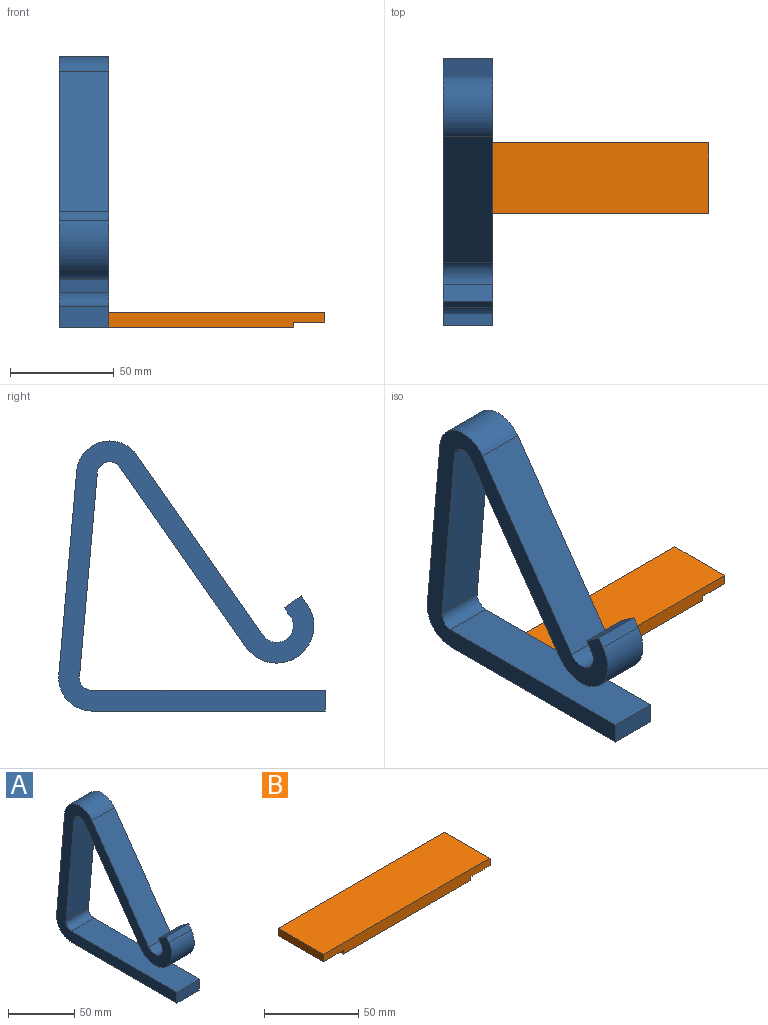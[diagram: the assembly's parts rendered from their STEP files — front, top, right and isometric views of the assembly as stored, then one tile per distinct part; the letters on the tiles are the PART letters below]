
ASSEMBLY  parts=2 mates=2
PART A: 28 faces, bbox 24x128.5x130.2 mm
  f0: plane 130.2x128.54mm, normal (1,0,0), area 3717.2mm2, adj f1,f2,f3,f4,f5,f6,f7,f8
  f1: plane 86.86x60.82mm, normal (0,0.82,-0.57), area 2545mm2, adj f0,f2,f13,f14
  f2: cylinder r=6mm len=24mm, axis (-1,0,0), area 351.9mm2, adj f0,f1,f3,f14
  f3: plane 98.2x24mm, normal (0,-1,-0.09), area 2365.9mm2, adj f0,f2,f4,f14
  f4: cylinder r=6mm len=24mm, axis (-1,0,0), area 238.8mm2, adj f0,f3,f5,f14
  f5: plane 112.54x24mm, normal (0,0,1), area 2700.9mm2, adj f0,f4,f6,f14
  f6: plane 24x10mm, normal (0,-1,0), area 240mm2, adj f0,f5,f7,f14
  f7: plane 112.54x24mm, normal (0,0,-1), area 2700.9mm2, adj f0,f6,f8,f14
  f8: cylinder r=16mm len=24mm, axis (-1,0,0), area 636.7mm2, adj f0,f7,f9,f14
  f9: plane 98.2x24mm, normal (0,1,0.09), area 2365.9mm2, adj f0,f8,f10,f14
  f10: cylinder r=16mm len=29.05mm, axis (-1,0,0), area 938.3mm2, adj f0,f9,f11,f14
  f11: plane 86.86x60.82mm, normal (0,-0.82,0.57), area 2545mm2, adj f0,f10,f12,f14
  f12: cylinder r=8mm len=24mm, axis (-1,0,0), area 603.2mm2, adj f0,f11,f14,f26
  f13: cylinder r=18mm len=32.74mm, axis (-1,0,0), area 1357.2mm2, adj f0,f1,f14,f25
  f14: plane 130.2x128.54mm, normal (-1,0,0), area 4081.2mm2, adj f1,f2,f3,f4,f5,f6,f7,f8
  f15: plane 34.87x20mm, normal (0,1,0.09), area 700mm2, adj f0,f16,f18,f19
  f16: plane 20x5.18mm, normal (0,-0.09,1), area 104mm2, adj f0,f15,f17,f19
  f17: plane 34.87x20mm, normal (0,-1,-0.09), area 700mm2, adj f0,f16,f18,f19
  f18: plane 20x5.18mm, normal (0,0.09,-1), area 104mm2, adj f0,f15,f17,f19
  f19: plane 35.32x8.23mm, normal (1,0,0), area 182mm2, adj f15,f16,f17,f18
  f20: plane 35x20mm, normal (0,0,-1), area 700mm2, adj f0,f21,f23,f24
  f21: plane 20x5.2mm, normal (0,1,0), area 104mm2, adj f0,f20,f22,f24
  f22: plane 35x20mm, normal (0,0,1), area 700mm2, adj f0,f21,f23,f24
  f23: plane 20x5.2mm, normal (0,-1,0), area 104mm2, adj f0,f20,f22,f24
  f24: plane 35x5.2mm, normal (1,0,0), area 182mm2, adj f20,f21,f22,f23
  f25: plane 24x4.1mm, normal (0,-0.82,0.57), area 120mm2, adj f0,f13,f14,f27
  f26: plane 24x4.1mm, normal (0,0.82,-0.57), area 120mm2, adj f0,f12,f14,f27
  f27: plane 24x8.19mm, normal (0,0.57,0.82), area 240mm2, adj f0,f14,f25,f26
PART B: 10 faces, bbox 125x34x7.2 mm
  f0: plane 125x34mm, normal (0,0,1), area 4250mm2, adj f1,f7,f8,f9
  f1: plane 34x4.8mm, normal (-1,0,0), area 163.2mm2, adj f0,f2,f8,f9
  f2: plane 34x15mm, normal (0,0,-1), area 510mm2, adj f1,f3,f8,f9
  f3: plane 34x2.4mm, normal (-1,0,0), area 81.6mm2, adj f2,f4,f8,f9
  f4: plane 95x34mm, normal (0,0,-1), area 3230mm2, adj f3,f5,f8,f9
  f5: plane 34x2.4mm, normal (1,0,0), area 81.6mm2, adj f4,f6,f8,f9
  f6: plane 34x15mm, normal (0,0,-1), area 510mm2, adj f5,f7,f8,f9
  f7: plane 34x4.8mm, normal (1,0,0), area 163.2mm2, adj f0,f6,f8,f9
  f8: plane 125x7.2mm, normal (0,-1,0), area 828mm2, adj f0,f1,f2,f3,f4,f5,f6,f7
  f9: plane 125x7.2mm, normal (0,1,0), area 828mm2, adj f0,f1,f2,f3,f4,f5,f6,f7
PLACE A at identity fixed
PLACE B t=(65.72,87.94,-0.14)mm
MATE planar B.f4 <-> A.f7  axis (0,0,-1) through (18.22,70.94,0)mm
MATE parallel B.f8 <-> A.f21  axis (0,-1,0) through (65.72,53.94,3.81)mm
